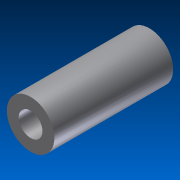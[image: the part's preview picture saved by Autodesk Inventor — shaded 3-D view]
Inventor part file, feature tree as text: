
AUTODESK INVENTOR PART (.ipt)
format: ipt  version: 2012 (Build 160160000, 160)  size: 80,896 bytes
history: native  units: in
note: dims shown in document units (in); Inventor stores cm internally (conversion verified against a paired STEP export)
features: extrude x1, sketch x1
ambient origin geometry x8: Origin, YZ Plane, XZ Plane, XY Plane, X Axis, Y Axis, Z Axis, Center Point
bodies: Solid1 (feature_tree)
feature tree (2):
  extrude  "Extrusion1"  Depth=0.2362in
  sketch  "Sketch1"  dims[d0=0.1181in d1=0.2362in d2=0.5906in d3=0.0in]
